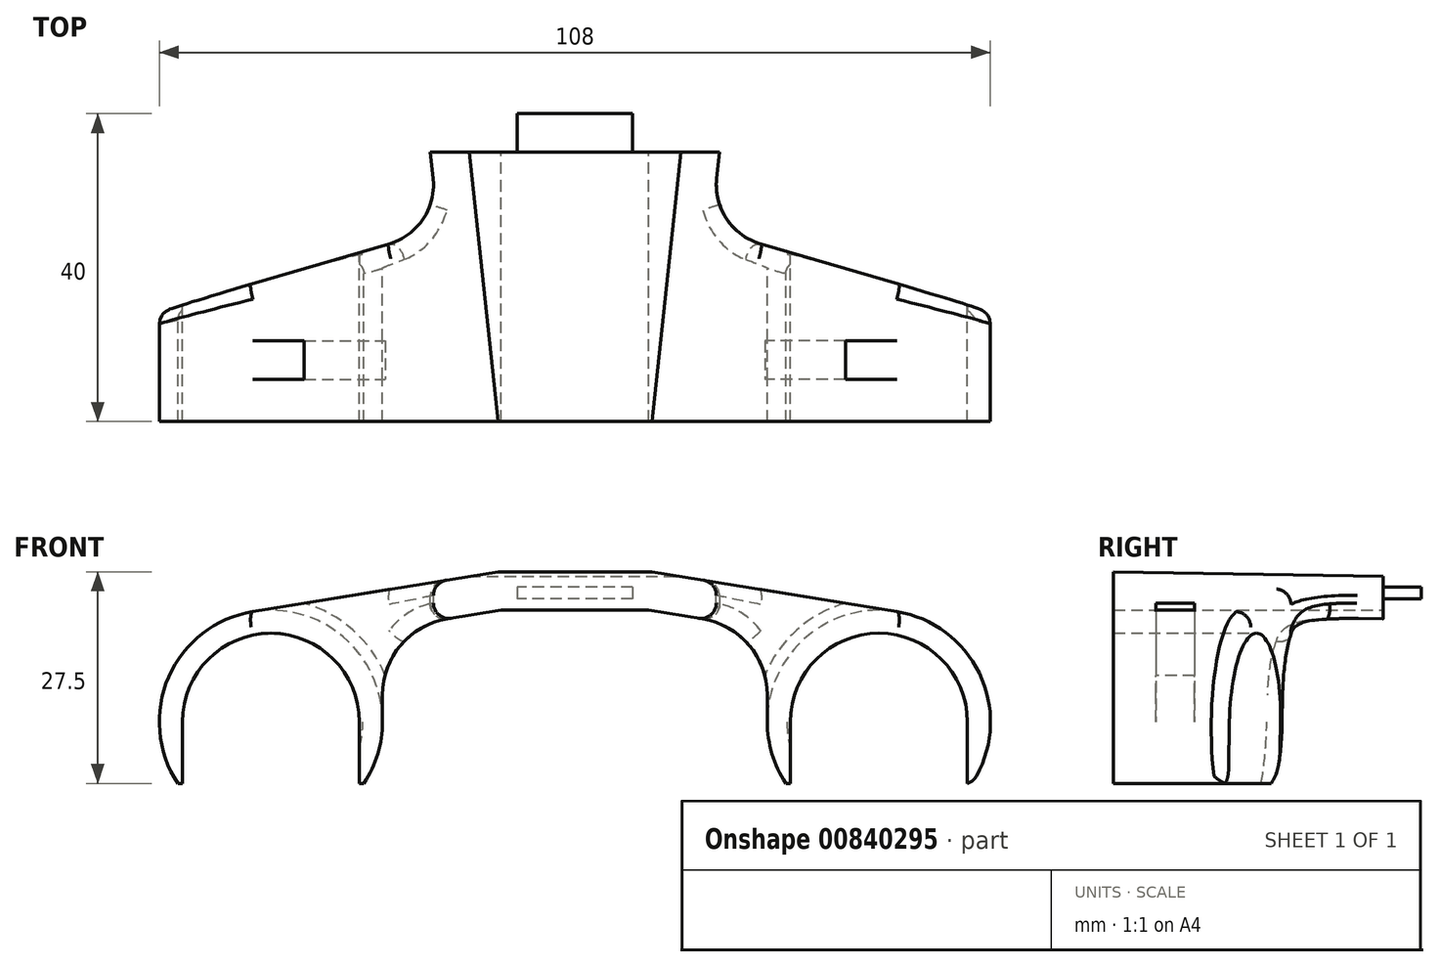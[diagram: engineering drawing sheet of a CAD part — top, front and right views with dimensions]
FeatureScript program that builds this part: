
annotation { "Feature Type Name" : "Feature", "Feature Type Description" : "" }
export const myFeature = defineFeature(function(context is Context, id is Id, definition is map)
    precondition{}
    {
        {
            var Q0;
            Q0=qCreatedBy(makeId("Front.planeOp"),FACE);
            var sketch = newSketch(context, id + "F0", { "sketchPlane" : qUnion([Q0])});
            skArc(sketch, "E0", {"start": v(51, 0) * mm, "mid": v(39.5, 11.5) * mm, "end": v(28, 0) * mm});
            skLineSegment(sketch, "E1", {"start": v(0, 0) * mm, "end": v(39.5, 0) * mm, "construction": true});
            skArc(sketch, "E2.0", {"start": v(51.6, -8) * mm, "mid": v(52.78, 5.81) * mm, "end": v(41.83, 14.31) * mm});
            skLineSegment(sketch, "E3", {"start": v(0, 19.5) * mm, "end": v(10, 19.5) * mm});
            skLineSegment(sketch, "E4", {"start": v(10, 19.5) * mm, "end": v(41.83, 14.31) * mm});
            skLineSegment(sketch, "E5.0", {"start": v(9.6, 14.5) * mm, "end": v(16.6, 13.36) * mm});
            skLineSegment(sketch, "E5.1", {"start": v(0, 14.5) * mm, "end": v(9.6, 14.5) * mm});
            skLineSegment(sketch, "E6", {"start": v(25, 0) * mm, "end": v(25, 3.49) * mm});
            skPoint(sketch, "E7.visualSharp", {"position": v(25, 11.99) * mm});
            skArc(sketch, "E7.filletArc", {"start": v(25, 3.49) * mm, "mid": v(22.62, 9.96) * mm, "end": v(16.6, 13.36) * mm});
            skLineSegment(sketch, "E8", {"start": v(27.4, -8) * mm, "end": v(28, -8) * mm});
            skLineSegment(sketch, "E9", {"start": v(28, 0) * mm, "end": v(28, -8) * mm});
            skLineSegment(sketch, "E10", {"start": v(51, 0) * mm, "end": v(51, -8) * mm});
            skLineSegment(sketch, "E11.trimOffspring", {"start": v(51, -8) * mm, "end": v(51.6, -8) * mm});
            skArc(sketch, "E12.trimOffspring", {"start": v(25, 0) * mm, "mid": v(25.61, -4.18) * mm, "end": v(27.4, -8) * mm});
            skLineSegment(sketch, "E13", {"start": v(0, 19.5) * mm, "end": v(0, 14.5) * mm});
            skSolve(sketch);
        }
        {
            var Q0;
            Q0=qSketchRegion(id+"F0",true);
            extrude(context, id + "F1", {"entities" : qUnion([Q0]), "endBound" : BoundingType.SYMMETRIC, "depth" : 70 * mm, "offsetDistance" : 25 * mm});
        }
        {
            var Q0;
            Q0=makeQuery(id+"F1.opExtrude","CAP_EDGE",EDGE,{"disambiguationData":[OSD([sQuery(id+"F0.wireOp",EDGE,"E3")])],"isStart":true});
            chamfer(context, id + "F2", {"entities" : qUnion([Q0]), "chamferType" : ChamferType.OFFSET_ANGLE, "width" : 70 * mm, "oppositeDirection" : true, "angle" : 1 * degree, "tangentPropagation" : true});
        }
        {
            var Q0;
            Q0=makeQuery(id+"F2.opChamfer","BLEND_FACE",FACE,{"disambiguationData":[OSD([sQuery(id+"F0.wireOp",EDGE,"E3")])]});
            var sketch = newSketch(context, id + "F3", { "sketchPlane" : qUnion([Q0])});
            skLineSegment(sketch, "E14", {"start": v(55, 21.6) * mm, "end": v(19.84, 9.57) * mm});
            skLineSegment(sketch, "E15", {"start": v(17.7, -10.33) * mm, "end": v(55, -21.1) * mm});
            skLineSegment(sketch, "E16", {"start": v(55, -21.1) * mm, "end": v(55, 21.6) * mm});
            skLineSegment(sketch, "E17", {"start": v(17.7, -10.33) * mm, "end": v(19.84, 9.57) * mm});
            skPoint(sketch, "E18.orphan", {"position": v(16.1, 8.29) * mm});
            skSolve(sketch);
        }
        {
            var Q0;
            Q0=makeQuery(id+"F3.imprint","IMPRINT",FACE,{"disambiguationData":[TD([[makeQuery(id+"F3.imprint","IMPRINT",EDGE,{"derivedFrom":sQuery(id+"F3.wireOp",EDGE,"E14")}),1.0]])]});
            extrude(context, id + "F4", {"entities" : qUnion([Q0]), "operationType" : NewBodyOperationType.REMOVE, "endBound" : BoundingType.THROUGH_ALL, "oppositeDirection" : true, "depth" : 25 * mm, "offsetDistance" : 25 * mm});
        }
        {
            var Q0;
            Q0=makeQuery(id+"F4.boolean.opBoolean","COPY",EDGE,{"derivedFrom":makeQuery(id+"F4.opExtrude","SWEPT_EDGE",EDGE,{"disambiguationData":[OSD([sQuery(id+"F3.wireOp",EDGE,"E14"),sQuery(id+"F3.wireOp",EDGE,"E17")])]})});
            var Q1;
            Q1=makeQuery(id+"F4.boolean.opBoolean","COPY",EDGE,{"derivedFrom":makeQuery(id+"F4.opExtrude","SWEPT_EDGE",EDGE,{"disambiguationData":[OSD([sQuery(id+"F3.wireOp",EDGE,"E15"),sQuery(id+"F3.wireOp",EDGE,"E17")])]})});
            fillet(context, id + "F5", {"entities" : qUnion([Q0, Q1]), "radius" : 8 * mm, "tangentPropagation" : true, "allowEdgeOverflow" : false});
        }
        {
            var Q0;
            {var subQ0=makeQuery(id+"F1.opExtrude","CAP_FACE",FACE,{"disambiguationData":[OSD([sQuery(id+"F0.wireOp",EDGE,"E0"),sQuery(id+"F0.wireOp",EDGE,"E2.0"),sQuery(id+"F0.wireOp",EDGE,"E3"),sQuery(id+"F0.wireOp",EDGE,"E4"),sQuery(id+"F0.wireOp",EDGE,"E5.0"),sQuery(id+"F0.wireOp",EDGE,"E5.1"),sQuery(id+"F0.wireOp",EDGE,"E6"),sQuery(id+"F0.wireOp",EDGE,"E7.filletArc"),sQuery(id+"F0.wireOp",EDGE,"E8"),sQuery(id+"F0.wireOp",EDGE,"E9"),sQuery(id+"F0.wireOp",EDGE,"E10"),sQuery(id+"F0.wireOp",EDGE,"E11.trimOffspring"),sQuery(id+"F0.wireOp",EDGE,"E12.trimOffspring"),sQuery(id+"F0.wireOp",EDGE,"E13")])],"isStart":false});Q0=makeQuery(id+"FHFeFmnZixUwJ2z_1.boolean.opBoolean","MERGE",FACE,{"derivedFrom":[subQ0,makeQuery(id+"FHFeFmnZixUwJ2z_1.opPattern","COPY",FACE,{"derivedFrom":subQ0,"instanceName":"1"})]});}
            cPlane(context, id + "F6", {"entities" : qUnion([Q0]), "cplaneType" : CPlaneType.OFFSET, "offset" : 8 * mm, "oppositeDirection" : true, "width" : 150 * mm, "height" : 150 * mm});
        }
        {
            var Q0;
            {var subQ0=makeQuery(id+"F1.opExtrude","CAP_FACE",FACE,{"disambiguationData":[OSD([sQuery(id+"F0.wireOp",EDGE,"E0"),sQuery(id+"F0.wireOp",EDGE,"E2.0"),sQuery(id+"F0.wireOp",EDGE,"E3"),sQuery(id+"F0.wireOp",EDGE,"E4"),sQuery(id+"F0.wireOp",EDGE,"E5.0"),sQuery(id+"F0.wireOp",EDGE,"E5.1"),sQuery(id+"F0.wireOp",EDGE,"E6"),sQuery(id+"F0.wireOp",EDGE,"E7.filletArc"),sQuery(id+"F0.wireOp",EDGE,"E8"),sQuery(id+"F0.wireOp",EDGE,"E9"),sQuery(id+"F0.wireOp",EDGE,"E10"),sQuery(id+"F0.wireOp",EDGE,"E11.trimOffspring"),sQuery(id+"F0.wireOp",EDGE,"E12.trimOffspring"),sQuery(id+"F0.wireOp",EDGE,"E13")])],"isStart":true});Q0=makeQuery(id+"FHFeFmnZixUwJ2z_1.boolean.opBoolean","MERGE",FACE,{"derivedFrom":[subQ0,makeQuery(id+"FHFeFmnZixUwJ2z_1.opPattern","COPY",FACE,{"derivedFrom":subQ0,"instanceName":"1"})]});}
            cPlane(context, id + "F7", {"entities" : qUnion([Q0]), "cplaneType" : CPlaneType.OFFSET, "offset" : 8 * mm, "oppositeDirection" : true, "width" : 150 * mm, "height" : 150 * mm});
        }
        {
            var Q0;
            Q0=qCreatedBy(id+"F6.planeOp",FACE);
            var sketch = newSketch(context, id + "F8", { "sketchPlane" : qUnion([Q0])});
            skArc(sketch, "E19.converted", {"start": v(41.83, 14.31) * mm, "mid": v(30.1, 11.05) * mm, "end": v(25, 0) * mm});
            skPoint(sketch, "E20.orphan", {"position": v(41.83, 14.31) * mm});
            skArc(sketch, "E21.0", {"start": v(35.16, 15.4) * mm, "mid": v(28.83, 11.92) * mm, "end": v(24.67, 6.02) * mm});
            skArc(sketch, "E22.0", {"start": v(25, 3.49) * mm, "mid": v(24.92, 4.76) * mm, "end": v(24.67, 6.02) * mm});
            skLineSegment(sketch, "E23.0", {"start": v(25, 0) * mm, "end": v(25, 3.49) * mm});
            skLineSegment(sketch, "E24.0", {"start": v(35.16, 15.4) * mm, "end": v(41.83, 14.31) * mm});
            skPoint(sketch, "E25.orphan", {"position": v(16.6, 13.36) * mm});
            skPoint(sketch, "E26.orphan", {"position": v(10, 19.5) * mm});
            skSolve(sketch);
        }
        {
            var Q0;
            Q0=qSketchRegion(id+"F8",true);
            extrude(context, id + "F9", {"entities" : qUnion([Q0]), "operationType" : NewBodyOperationType.REMOVE, "endBound" : BoundingType.SYMMETRIC, "oppositeDirection" : true, "depth" : 5 * mm, "offsetDistance" : 25 * mm});
        }
        {
            var Q0;
            Q0=qCreatedBy(id+"F7.planeOp",FACE);
            var sketch = newSketch(context, id + "F10", { "sketchPlane" : qUnion([Q0])});
            skArc(sketch, "E27.converted", {"start": v(-41.83, 14.31) * mm, "mid": v(-30.1, 11.05) * mm, "end": v(-25, 0) * mm});
            skPoint(sketch, "E28.orphan", {"position": v(-41.83, 14.31) * mm});
            skLineSegment(sketch, "E29.0", {"start": v(-35.16, 15.4) * mm, "end": v(-41.83, 14.31) * mm});
            skLineSegment(sketch, "E30.0", {"start": v(-25, 0) * mm, "end": v(-25, 3.49) * mm});
            skArc(sketch, "E31.0", {"start": v(-25, 3.49) * mm, "mid": v(-24.92, 4.76) * mm, "end": v(-24.67, 6.02) * mm});
            skArc(sketch, "E32.0", {"start": v(-35.16, 15.4) * mm, "mid": v(-28.83, 11.92) * mm, "end": v(-24.67, 6.02) * mm});
            skPoint(sketch, "E33.orphan", {"position": v(-17.5, 18.28) * mm});
            skPoint(sketch, "E34.orphan", {"position": v(-16.6, 13.36) * mm});
            skSolve(sketch);
        }
        {
            var Q0;
            Q0=qSketchRegion(id+"F10",true);
            extrude(context, id + "F11", {"entities" : qUnion([Q0]), "operationType" : NewBodyOperationType.REMOVE, "endBound" : BoundingType.SYMMETRIC, "oppositeDirection" : true, "depth" : 5 * mm, "offsetDistance" : 25 * mm});
        }
        {
            var Q0;
            Q0=makeQuery(id+"F1.opExtrude","SWEPT_BODY",BODY,{"disambiguationData":[OSD([sQuery(id+"F0.wireOp",EDGE,"E0"),sQuery(id+"F0.wireOp",EDGE,"E2.0"),sQuery(id+"F0.wireOp",EDGE,"E3"),sQuery(id+"F0.wireOp",EDGE,"E4"),sQuery(id+"F0.wireOp",EDGE,"E5.0"),sQuery(id+"F0.wireOp",EDGE,"E5.1"),sQuery(id+"F0.wireOp",EDGE,"E6"),sQuery(id+"F0.wireOp",EDGE,"E7.filletArc"),sQuery(id+"F0.wireOp",EDGE,"E8"),sQuery(id+"F0.wireOp",EDGE,"E9"),sQuery(id+"F0.wireOp",EDGE,"E10"),sQuery(id+"F0.wireOp",EDGE,"E11.trimOffspring"),sQuery(id+"F0.wireOp",EDGE,"E12.trimOffspring"),sQuery(id+"F0.wireOp",EDGE,"E13")])]});
            var Q1;
            Q1=makeQuery(id+"F1.opExtrude","SWEPT_FACE",FACE,{"disambiguationData":[OSD([sQuery(id+"F0.wireOp",EDGE,"E13")])]});
            mirror(context, id + "F12", {"operationType" : NewBodyOperationType.ADD, "entities" : qUnion([Q0]), "mirrorPlane" : qUnion([Q1])});
        }
        {
            var Q0;
            Q0=makeQuery(id+"F4.boolean.opBoolean","INTERSECT",EDGE,{"derivedFrom":[makeQuery(id+"F1.opExtrude","SWEPT_FACE",FACE,{"disambiguationData":[OSD([sQuery(id+"F0.wireOp",EDGE,"E4")])]}),makeQuery(id+"F4.opExtrude","SWEPT_FACE",FACE,{"disambiguationData":[OSD([sQuery(id+"F3.wireOp",EDGE,"E17")])]})]});
            var Q1;
            Q1=makeQuery(id+"F12.opPattern","COPY",EDGE,{"derivedFrom":makeQuery(id+"F4.boolean.opBoolean","INTERSECT",EDGE,{"derivedFrom":[makeQuery(id+"F1.opExtrude","SWEPT_FACE",FACE,{"disambiguationData":[OSD([sQuery(id+"F0.wireOp",EDGE,"E4")])]}),makeQuery(id+"F4.opExtrude","SWEPT_FACE",FACE,{"disambiguationData":[OSD([sQuery(id+"F3.wireOp",EDGE,"E17")])]})]}),"instanceName":"1"});
            var Q2;
            {var subQ0=sQuery(id+"F0.wireOp",EDGE,"E11.trimOffspring");var subQ1=sQuery(id+"F0.wireOp",EDGE,"E2.0");Q2=makeQuery(id+"F4.boolean.opBoolean","SPLIT",EDGE,{"disambiguationData":[TD([makeQuery(id+"F4.opExtrude","SWEPT_FACE",FACE,{"disambiguationData":[OSD([sQuery(id+"F3.wireOp",EDGE,"E15")])]})])],"derivedFrom":makeQuery(id+"F1.opExtrude","SWEPT_EDGE",EDGE,{"disambiguationData":[OSD([subQ1,subQ0])]})});}
            var Q3;
            {var subQ0=sQuery(id+"F0.wireOp",EDGE,"E11.trimOffspring");var subQ1=sQuery(id+"F0.wireOp",EDGE,"E2.0");Q3=makeQuery(id+"F4.boolean.opBoolean","SPLIT",EDGE,{"disambiguationData":[TD([makeQuery(id+"F4.opExtrude","SWEPT_FACE",FACE,{"disambiguationData":[OSD([sQuery(id+"F3.wireOp",EDGE,"E14")])]})])],"derivedFrom":makeQuery(id+"F1.opExtrude","SWEPT_EDGE",EDGE,{"disambiguationData":[OSD([subQ1,subQ0])]})});}
            var Q4;
            Q4=makeQuery(id+"F4.boolean.opBoolean","INTERSECT",EDGE,{"derivedFrom":[makeQuery(id+"F1.opExtrude","SWEPT_FACE",FACE,{"disambiguationData":[OSD([sQuery(id+"F0.wireOp",EDGE,"E7.filletArc")])]}),makeQuery(id+"F4.opExtrude","SWEPT_FACE",FACE,{"disambiguationData":[OSD([sQuery(id+"F3.wireOp",EDGE,"E17")])]})]});
            var Q5;
            Q5=makeQuery(id+"F4.boolean.opBoolean","INTERSECT",EDGE,{"derivedFrom":[makeQuery(id+"F1.opExtrude","SWEPT_FACE",FACE,{"disambiguationData":[OSD([sQuery(id+"F0.wireOp",EDGE,"E12.trimOffspring")])]}),makeQuery(id+"F4.opExtrude","SWEPT_FACE",FACE,{"disambiguationData":[OSD([sQuery(id+"F3.wireOp",EDGE,"E14")])]})]});
            var Q6;
            Q6=makeQuery(id+"F4.boolean.opBoolean","INTERSECT",EDGE,{"derivedFrom":[makeQuery(id+"F1.opExtrude","SWEPT_FACE",FACE,{"disambiguationData":[OSD([sQuery(id+"F0.wireOp",EDGE,"E6")])]}),makeQuery(id+"F4.opExtrude","SWEPT_FACE",FACE,{"disambiguationData":[OSD([sQuery(id+"F3.wireOp",EDGE,"E14")])]})]});
            var Q7;
            Q7=makeQuery(id+"F4.boolean.opBoolean","INTERSECT",EDGE,{"derivedFrom":[makeQuery(id+"F1.opExtrude","SWEPT_FACE",FACE,{"disambiguationData":[OSD([sQuery(id+"F0.wireOp",EDGE,"E7.filletArc")])]}),makeQuery(id+"F4.opExtrude","SWEPT_FACE",FACE,{"disambiguationData":[OSD([sQuery(id+"F3.wireOp",EDGE,"E14")])]})]});
            var Q8;
            Q8=makeQuery(id+"F5.opFillet","BLEND_EDGE",EDGE,{"blendedFrom":[makeQuery(id+"F4.boolean.opBoolean","COPY",EDGE,{"derivedFrom":makeQuery(id+"F4.opExtrude","SWEPT_EDGE",EDGE,{"disambiguationData":[OSD([sQuery(id+"F3.wireOp",EDGE,"E14"),sQuery(id+"F3.wireOp",EDGE,"E17")])]})}),makeQuery(id+"F1.opExtrude","SWEPT_FACE",FACE,{"disambiguationData":[OSD([sQuery(id+"F0.wireOp",EDGE,"E7.filletArc")])]})],"blendedInto":[makeQuery(id+"F1.opExtrude","SWEPT_FACE",FACE,{"disambiguationData":[OSD([sQuery(id+"F0.wireOp",EDGE,"E7.filletArc")])]})]});
            var Q9;
            Q9=makeQuery(id+"F5.opFillet","BLEND_EDGE",EDGE,{"blendedFrom":[makeQuery(id+"F4.boolean.opBoolean","COPY",EDGE,{"derivedFrom":makeQuery(id+"F4.opExtrude","SWEPT_EDGE",EDGE,{"disambiguationData":[OSD([sQuery(id+"F3.wireOp",EDGE,"E15"),sQuery(id+"F3.wireOp",EDGE,"E17")])]})}),makeQuery(id+"F1.opExtrude","SWEPT_FACE",FACE,{"disambiguationData":[OSD([sQuery(id+"F0.wireOp",EDGE,"E7.filletArc")])]})],"blendedInto":[makeQuery(id+"F1.opExtrude","SWEPT_FACE",FACE,{"disambiguationData":[OSD([sQuery(id+"F0.wireOp",EDGE,"E7.filletArc")])]})]});
            var Q10;
            Q10=makeQuery(id+"F4.boolean.opBoolean","INTERSECT",EDGE,{"derivedFrom":[makeQuery(id+"F1.opExtrude","SWEPT_FACE",FACE,{"disambiguationData":[OSD([sQuery(id+"F0.wireOp",EDGE,"E7.filletArc")])]}),makeQuery(id+"F4.opExtrude","SWEPT_FACE",FACE,{"disambiguationData":[OSD([sQuery(id+"F3.wireOp",EDGE,"E15")])]})]});
            var Q11;
            Q11=makeQuery(id+"F4.boolean.opBoolean","INTERSECT",EDGE,{"derivedFrom":[makeQuery(id+"F1.opExtrude","SWEPT_FACE",FACE,{"disambiguationData":[OSD([sQuery(id+"F0.wireOp",EDGE,"E6")])]}),makeQuery(id+"F4.opExtrude","SWEPT_FACE",FACE,{"disambiguationData":[OSD([sQuery(id+"F3.wireOp",EDGE,"E15")])]})]});
            var Q12;
            Q12=makeQuery(id+"F4.boolean.opBoolean","INTERSECT",EDGE,{"derivedFrom":[makeQuery(id+"F1.opExtrude","SWEPT_FACE",FACE,{"disambiguationData":[OSD([sQuery(id+"F0.wireOp",EDGE,"E12.trimOffspring")])]}),makeQuery(id+"F4.opExtrude","SWEPT_FACE",FACE,{"disambiguationData":[OSD([sQuery(id+"F3.wireOp",EDGE,"E15")])]})]});
            var Q13;
            Q13=makeQuery(id+"F12.opPattern","COPY",EDGE,{"derivedFrom":makeQuery(id+"F4.boolean.opBoolean","INTERSECT",EDGE,{"derivedFrom":[makeQuery(id+"F1.opExtrude","SWEPT_FACE",FACE,{"disambiguationData":[OSD([sQuery(id+"F0.wireOp",EDGE,"E7.filletArc")])]}),makeQuery(id+"F4.opExtrude","SWEPT_FACE",FACE,{"disambiguationData":[OSD([sQuery(id+"F3.wireOp",EDGE,"E17")])]})]}),"instanceName":"1"});
            fillet(context, id + "F13", {"entities" : qUnion([Q0, Q1, Q2, Q3, Q4, Q5, Q6, Q7, Q8, Q9, Q10, Q11, Q12, Q13]), "radius" : 2 * mm, "tangentPropagation" : true, "allowEdgeOverflow" : false});
        }
        {
            var Q0;
            Q0=qCreatedBy(makeId("Top.planeOp"),FACE);
            var sketch = newSketch(context, id + "F14", { "sketchPlane" : qUnion([Q0])});
            skLineSegment(sketch, "E35.bottom", {"start": v(-60, 40) * mm, "end": v(60, 40) * mm});
            skLineSegment(sketch, "E35.top", {"start": v(-60, 0) * mm, "end": v(60, 0) * mm});
            skLineSegment(sketch, "E35.left", {"start": v(-60, 40) * mm, "end": v(-60, 0) * mm});
            skLineSegment(sketch, "E35.right", {"start": v(60, 40) * mm, "end": v(60, 0) * mm});
            skSolve(sketch);
        }
        {
            var Q0;
            Q0=makeQuery(id+"F14.imprint","IMPRINT",FACE,{"disambiguationData":[TD([[makeQuery(id+"F14.imprint","IMPRINT",EDGE,{"derivedFrom":sQuery(id+"F14.wireOp",EDGE,"E35.bottom")}),-1.0]])]});
            extrude(context, id + "F15", {"entities" : qUnion([Q0]), "operationType" : NewBodyOperationType.REMOVE, "endBound" : BoundingType.SYMMETRIC, "oppositeDirection" : true, "depth" : 40 * mm, "offsetDistance" : 25 * mm});
        }
        {
            var Q0;
            Q0=makeQuery(id+"F15.boolean.opBoolean","COPY",FACE,{"derivedFrom":makeQuery(id+"F15.opExtrude","SWEPT_FACE",FACE,{"disambiguationData":[OSD([sQuery(id+"F14.wireOp",EDGE,"E35.top")])]})});
            var sketch = newSketch(context, id + "F16", { "sketchPlane" : qUnion([Q0])});
            skLineSegment(sketch, "E36.bottom", {"start": v(-7.5, 17.5) * mm, "end": v(7.5, 17.5) * mm});
            skLineSegment(sketch, "E36.top", {"start": v(-7.5, 16) * mm, "end": v(7.5, 16) * mm});
            skLineSegment(sketch, "E36.left", {"start": v(-7.5, 17.5) * mm, "end": v(-7.5, 16) * mm});
            skLineSegment(sketch, "E36.right", {"start": v(7.5, 17.5) * mm, "end": v(7.5, 16) * mm});
            skSolve(sketch);
        }
        {
            var Q0;
            Q0=makeQuery(id+"F16.imprint","IMPRINT",FACE,{"disambiguationData":[TD([[makeQuery(id+"F16.imprint","IMPRINT",EDGE,{"derivedFrom":sQuery(id+"F16.wireOp",EDGE,"E36.bottom")}),-1.0]])]});
            extrude(context, id + "F17", {"entities" : qUnion([Q0]), "operationType" : NewBodyOperationType.ADD, "depth" : 5 * mm, "offsetDistance" : 25 * mm});
        }
    });
